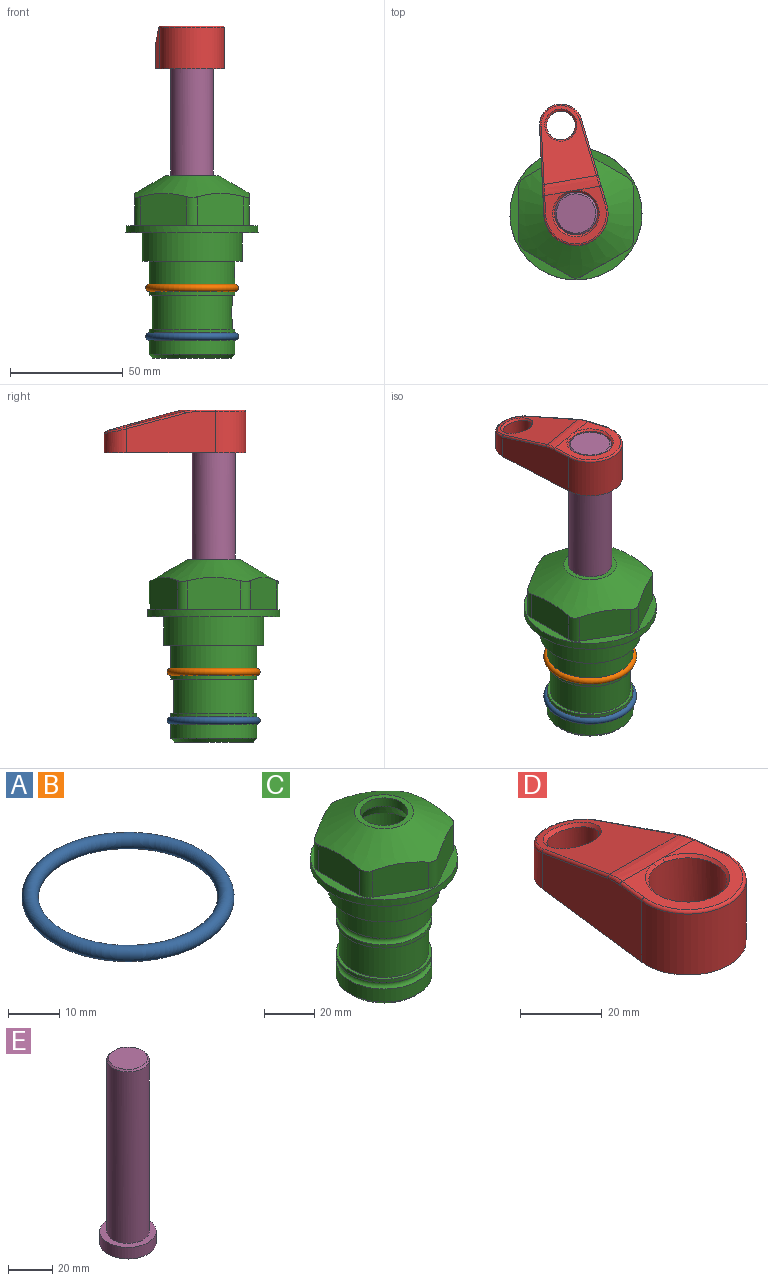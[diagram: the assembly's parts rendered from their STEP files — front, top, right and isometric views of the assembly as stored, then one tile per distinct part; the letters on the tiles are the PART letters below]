
ASSEMBLY  parts=5 mates=4
PART A: 1 faces, bbox 44.7x44.7x3.2 mm
  f0: torus R=19.05mm, axis (0,0,1), area 1193.9mm2
PART B: same geometry as A
PART C: 36 faces, bbox 58.7x58.7x81 mm
  f0: cylinder r=17.78mm len=35.56mm, axis (0,0,1), area 1670.8mm2, adj f23,f24,f31
  f1: cylinder r=19.05mm len=38.1mm, axis (0,0,1), area 1191.9mm2, adj f26,f27,f30
  f2: plane 58.66x58.66mm, normal (0,0,-1), area 1150.6mm2, adj f3,f28
  f3: cylinder r=29.33mm len=58.66mm, axis (0,0,-1), area 585.1mm2, adj f2,f4
  f4: plane 58.66x58.66mm, normal (0,0,1), area 475.9mm2, adj f3,f5,f6,f7,f8,f9,f10,f11
  f5: plane 20.32x14.34mm, normal (-0.5,0.87,0), area 324.4mm2, adj f4,f15,f16,f17
  f6: plane 20.32x14.34mm, normal (0.5,0.87,0), area 324.4mm2, adj f4,f14,f15,f17
  f7: plane 23.48x14.34mm, normal (1,0,0), area 324.4mm2, adj f4,f13,f14,f17
  f8: plane 20.32x14.34mm, normal (0.5,-0.87,0), area 324.4mm2, adj f4,f12,f13,f17
  f9: plane 20.32x14.34mm, normal (-0.5,-0.87,0), area 324.4mm2, adj f4,f11,f12,f17
  f10: plane 23.48x14.34mm, normal (-1,0,0), area 324.4mm2, adj f4,f11,f16,f17
  f11: cylinder r=5.08mm len=12.85mm, axis (0,0,-1), area 67.2mm2, adj f4,f9,f10,f17
  f12: cylinder r=5.08mm len=12.85mm, axis (0,0,-1), area 67.2mm2, adj f4,f8,f9,f17
  f13: cylinder r=5.08mm len=12.85mm, axis (0,0,-1), area 67.2mm2, adj f4,f7,f8,f17
  f14: cylinder r=5.08mm len=12.85mm, axis (0,0,-1), area 67.2mm2, adj f4,f6,f7,f17
  f15: cylinder r=5.08mm len=12.85mm, axis (0,0,-1), area 67.2mm2, adj f4,f5,f6,f17
  f16: cylinder r=5.08mm len=12.85mm, axis (0,0,-1), area 67.2mm2, adj f4,f5,f10,f17
  f17: cone r=11.73mm half-angle=60deg, axis (0,0,-1), area 2071.8mm2, adj f5,f6,f7,f8,f9,f10,f11,f12
  f18: plane 23.46x23.46mm, normal (0,0,1), area 147.4mm2, adj f17,f35
  f19: plane 34.93x34.93mm, normal (0,0,-1), area 958mm2, adj f29
  f20: cylinder r=19.05mm len=38.1mm, axis (0,0,1), area 760.1mm2, adj f21,f29
  f21: torus R=19.05mm, axis (0,0,1), area 565.3mm2, adj f20,f22
  f22: cylinder r=19.05mm len=38.1mm, axis (0,0,1), area 190mm2, adj f21,f23
  f23: plane 38.1x38.1mm, normal (0,0,1), area 146.9mm2, adj f0,f22
  f24: plane 38.1x38.1mm, normal (0,0,-1), area 146.9mm2, adj f0,f25
  f25: cylinder r=19.05mm len=38.1mm, axis (0,0,1), area 190mm2, adj f24,f26
  f26: torus R=19.05mm, axis (0,0,1), area 565.3mm2, adj f1,f25
  f27: plane 44.45x44.45mm, normal (0,0,-1), area 411.7mm2, adj f1,f28
  f28: cylinder r=22.23mm len=44.45mm, axis (0,0,1), area 1773.5mm2, adj f2,f27
  f29: cone r=19.05mm half-angle=45deg, axis (0,0,1), area 257.5mm2, adj f19,f20
  f30: cylinder r=3.17mm len=6.75mm, axis (-1,0,0), area 128mm2, adj f1,f33
  f31: cylinder r=3.17mm len=6.35mm, axis (-1,0,0), area 102.5mm2, adj f0,f33
  f32: plane 25.4x25.4mm, normal (0,0,1), area 506.7mm2, adj f33
  f33: cylinder r=12.7mm len=66.42mm, axis (0,0,-1), area 5236.2mm2, adj f30,f31,f32,f34
  f34: cone r=9.53mm half-angle=30deg, axis (0,0,-1), area 443.4mm2, adj f33,f35
  f35: cylinder r=9.53mm len=19.05mm, axis (0,0,-1), area 240.9mm2, adj f18,f34
PART D: 31 faces, bbox 31.7x65.5x19.8 mm
  f0: plane 39.12x18.26mm, normal (0.99,0.12,0), area 612.2mm2, adj f1,f4,f7,f11,f13,f15
  f1: cylinder r=9.53mm len=18.91mm, axis (0,0,-1), area 296.1mm2, adj f0,f2,f7,f17
  f2: plane 39.12x18.26mm, normal (-0.99,0.12,0), area 612.2mm2, adj f1,f4,f7,f12,f14,f16
  f3: cylinder r=6.35mm len=12.7mm, axis (0,0,-1), area 362.4mm2, adj f7,f18
  f4: cylinder r=14.29mm len=28.58mm, axis (0,0,-1), area 882.2mm2, adj f0,f2,f7,f10
  f5: cylinder r=9.53mm len=19.05mm, axis (0,0,-1), area 1092.6mm2, adj f7,f19,f20
  f6: plane 26.99x23.69mm, normal (0,0,1), area 216.2mm2, adj f9,f10,f11,f12,f19
  f7: plane 63.5x28.58mm, normal (0,0,-1), area 661.8mm2, adj f0,f1,f2,f3,f4,f5,f22,f23
  f8: plane 33.52x23.6mm, normal (0,0.26,0.97), area 486mm2, adj f9,f15,f16,f17,f18
  f9: cylinder r=19.05mm len=24.72mm, axis (1,0,0), area 120.4mm2, adj f6,f8,f13,f14,f20
  f10: torus R=13.49mm, axis (0,0,1), area 59mm2, adj f4,f6,f11,f12
  f11: cylinder r=0.79mm len=8.67mm, axis (0.12,-0.99,0), area 10.8mm2, adj f0,f6,f10,f13
  f12: cylinder r=0.79mm len=8.67mm, axis (0.12,0.99,0), area 10.8mm2, adj f2,f6,f10,f14
  f13: bspline ~4.95x1.42mm, area 6.1mm2, adj f0,f9,f11,f15
  f14: bspline ~4.95x1.42mm, area 6.1mm2, adj f2,f9,f12,f16
  f15: cylinder r=0.79mm len=25.95mm, axis (0.12,-0.96,0.26), area 32.9mm2, adj f0,f8,f13,f17
  f16: cylinder r=0.79mm len=25.95mm, axis (0.12,0.96,-0.26), area 32.9mm2, adj f2,f8,f14,f17
  f17: bspline ~18.91x8.38mm, area 30mm2, adj f1,f8,f15,f16
  f18: bspline ~14.29x14.29mm, area 48.3mm2, adj f3,f8
  f19: cone r=9.53mm half-angle=45deg, axis (0,0,1), area 66.5mm2, adj f5,f6,f20
  f20: bspline ~3.22x0.96mm, area 3.5mm2, adj f5,f9,f19
  f21: plane 2.75x2.72mm, normal (0,0,-1), area 2.9mm2, adj f23,f25,f28
  f22: plane 23.05x15.88mm, normal (-0.99,-0.12,0), area 323.6mm2, adj f7,f25,f26,f27,f28,f29
  f23: plane 23.05x15.88mm, normal (0.99,-0.12,0), area 323.6mm2, adj f7,f21,f25,f27,f28,f30
  f24: cylinder r=9.53mm len=10.69mm, axis (0,0,-1), area 114.7mm2, adj f7,f27,f29,f30
  f25: cylinder r=12.7mm len=20.59mm, axis (0,0,-1), area 381.1mm2, adj f7,f21,f22,f23,f26,f28
  f26: plane 2.75x2.72mm, normal (0,0,-1), area 2.9mm2, adj f22,f25,f28
  f27: plane 19.72x18.37mm, normal (0,-0.26,-0.97), area 291.8mm2, adj f22,f23,f24,f28,f29,f30
  f28: cylinder r=15.88mm len=19.92mm, axis (1,0,0), area 54.8mm2, adj f21,f22,f23,f25,f26,f27
  f29: cylinder r=1.59mm len=11mm, axis (0,0,-1), area 34.7mm2, adj f7,f22,f24,f27
  f30: cylinder r=1.59mm len=11mm, axis (0,0,-1), area 34.7mm2, adj f7,f23,f24,f27
PART E: 6 faces, bbox 25.4x25.4x101.6 mm
  f0: plane 17.46x17.46mm, normal (0,0,1), area 239.5mm2, adj f5
  f1: plane 25.4x25.4mm, normal (0,0,-1), area 506.7mm2, adj f2
  f2: cylinder r=12.7mm len=25.4mm, axis (0,0,1), area 506.7mm2, adj f1,f3
  f3: plane 25.4x25.4mm, normal (0,0,1), area 221.7mm2, adj f2,f4
  f4: cylinder r=9.53mm len=94.46mm, axis (0,0,1), area 5653mm2, adj f3,f5
  f5: cone r=8.73mm half-angle=45deg, axis (0,0,-1), area 64.4mm2, adj f0,f4
PLACE A t=(0,0,-21.59)mm
PLACE B at identity
PLACE C at identity fixed
PLACE D rot(axis=(0,0,1),9.7deg) t=(0,0,28.35)mm
PLACE E rot(axis=(0,0,1),9.7deg) t=(0,0,27.55)mm
MATE fastened B.f0 <-> C.f0  axis (0,0,1) through (0,0,-24.51)mm
MATE fastened A.f0 <-> C.f0  axis (0,0,1) through (0,0,-46.1)mm
MATE fastened E.f2 <-> D.f4  axis (0,0,1) through (0,0,91.05)mm
MATE cylindrical E.f2 <-> C.f0  axis (0,0,-1) through (0,0,-10.55)mm
